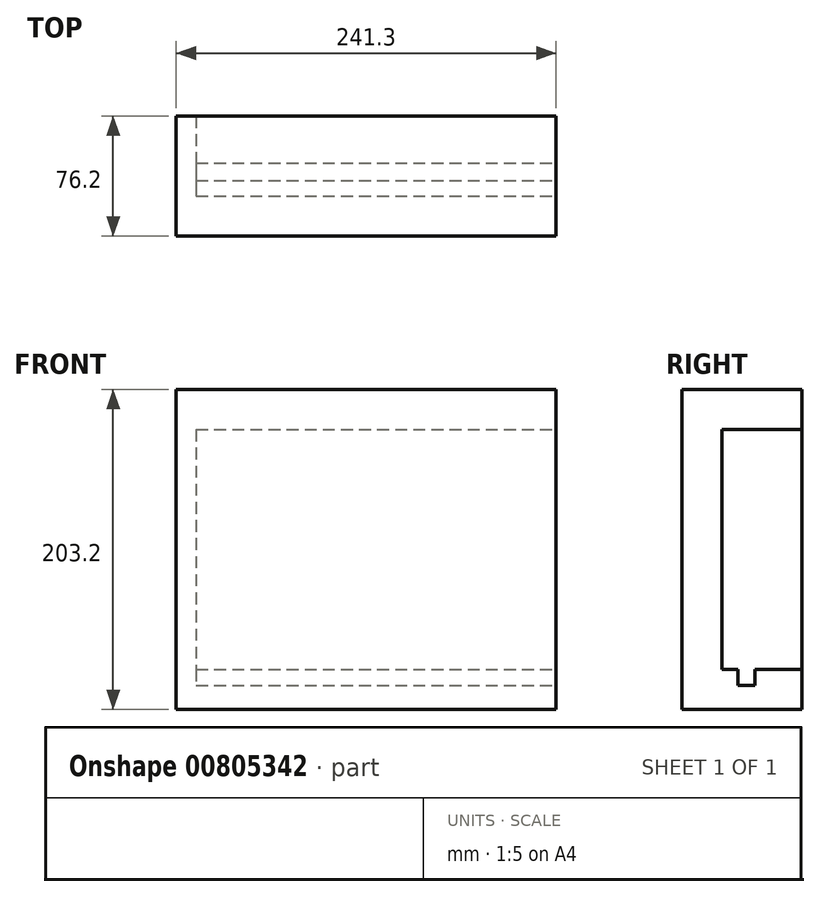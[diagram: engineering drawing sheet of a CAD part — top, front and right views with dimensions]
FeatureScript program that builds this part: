
annotation { "Feature Type Name" : "Feature", "Feature Type Description" : "" }
export const myFeature = defineFeature(function(context is Context, id is Id, definition is map)
    precondition{}
    {
        {
            var Q0;
            Q0=qCreatedBy(makeId("Top.planeOp"),FACE);
            var sketch = newSketch(context, id + "F0", { "sketchPlane" : qUnion([Q0])});
            skLineSegment(sketch, "E0.right", {"start": v(97.44, -125.76) * mm, "end": v(97.44, 52.04) * mm});
            skLineSegment(sketch, "E1.bottom", {"start": v(-131.16, 26.64) * mm, "end": v(97.44, 26.64) * mm});
            skLineSegment(sketch, "E1.top", {"start": v(-131.16, -24.16) * mm, "end": v(97.44, -24.16) * mm});
            skLineSegment(sketch, "E1.left", {"start": v(-131.16, 26.64) * mm, "end": v(-131.16, -24.16) * mm});
            skLineSegment(sketch, "E1.right", {"start": v(97.44, 26.64) * mm, "end": v(97.44, -24.16) * mm});
            skLineSegment(sketch, "E2.right", {"start": v(97.44, -49.56) * mm, "end": v(97.44, -100.36) * mm});
            skLineSegment(sketch, "E3.right", {"start": v(97.44, -80.36) * mm, "end": v(97.44, -90.36) * mm});
            skLineSegment(sketch, "E4.bottom", {"start": v(-131.16, -14.16) * mm, "end": v(97.44, -14.16) * mm});
            skLineSegment(sketch, "E4.top", {"start": v(-131.16, -3.16) * mm, "end": v(97.44, -3.16) * mm});
            skLineSegment(sketch, "E4.left", {"start": v(-131.16, -14.16) * mm, "end": v(-131.16, -3.16) * mm});
            skLineSegment(sketch, "E4.right", {"start": v(97.44, -14.16) * mm, "end": v(97.44, -3.16) * mm});
            skLineSegment(sketch, "E5.top", {"start": v(-143.86, -49.56) * mm, "end": v(97.44, -49.56) * mm});
            skLineSegment(sketch, "E5.right", {"start": v(97.44, 64.74) * mm, "end": v(97.44, -49.56) * mm});
            skLineSegment(sketch, "E6", {"start": v(-131.16, 26.64) * mm, "end": v(-143.86, 26.64) * mm});
            skLineSegment(sketch, "E7", {"start": v(-143.86, 26.64) * mm, "end": v(-143.86, -49.56) * mm});
            skSolve(sketch);
        }
        {
            var Q0;
            {var subQ0=sQuery(id+"F0.wireOp",EDGE,"E0.bottom");Q0=makeQuery(id+"F0.imprint","IMPRINT",FACE,{"disambiguationData":[TD([[makeQuery(id+"F0.imprint","IMPRINT",EDGE,{"derivedFrom":subQ0}),1.0]])]});}
            var Q1;
            {var subQ0=sQuery(id+"F0.wireOp",EDGE,"E1.top");Q1=makeQuery(id+"F0.imprint","IMPRINT",FACE,{"disambiguationData":[TD([[makeQuery(id+"F0.imprint","IMPRINT",EDGE,{"derivedFrom":subQ0}),-1.0]])]});}
            var Q2;
            {var subQ0=sQuery(id+"F0.wireOp",EDGE,"E0.top");Q2=makeQuery(id+"F0.imprint","IMPRINT",FACE,{"disambiguationData":[TD([[makeQuery(id+"F0.imprint","IMPRINT",EDGE,{"derivedFrom":subQ0}),-1.0]])]});}
            extrude(context, id + "F1", {"entities" : qUnion([Q0, Q1, Q2]), "depth" : 203.2 * mm, "offsetDistance" : 25.4 * mm});
        }
        {
            var Q0;
            {var subQ0=sQuery(id+"F0.wireOp",EDGE,"E2.top");Q0=makeQuery(id+"F0.imprint","IMPRINT",FACE,{"disambiguationData":[TD([[makeQuery(id+"F0.imprint","IMPRINT",EDGE,{"derivedFrom":subQ0}),1.0]])]});}
            var Q1;
            {var subQ0=sQuery(id+"F0.wireOp",EDGE,"E2.bottom");Q1=makeQuery(id+"F0.imprint","IMPRINT",FACE,{"disambiguationData":[TD([[makeQuery(id+"F0.imprint","IMPRINT",EDGE,{"derivedFrom":subQ0}),-1.0]])]});}
            var Q2;
            {var subQ0=sQuery(id+"F0.wireOp",EDGE,"E1.top");Q2=makeQuery(id+"F0.imprint","IMPRINT",FACE,{"disambiguationData":[TD([[makeQuery(id+"F0.imprint","IMPRINT",EDGE,{"derivedFrom":subQ0}),1.0]])]});}
            var Q3;
            {var subQ0=sQuery(id+"F0.wireOp",EDGE,"E1.bottom");Q3=makeQuery(id+"F0.imprint","IMPRINT",FACE,{"disambiguationData":[TD([[makeQuery(id+"F0.imprint","IMPRINT",EDGE,{"derivedFrom":subQ0}),-1.0]])]});}
            extrude(context, id + "F2", {"entities" : qUnion([Q0, Q1, Q2, Q3]), "depth" : 25.4 * mm, "offsetDistance" : 25.4 * mm});
        }
        {
            var Q0;
            Q0=makeQuery(id+"F0.imprint","IMPRINT",FACE,{"disambiguationData":[TD([[makeQuery(id+"F0.imprint","IMPRINT",EDGE,{"derivedFrom":sQuery(id+"F0.wireOp",EDGE,"E3.bottom")}),-1.0]])]});
            var Q1;
            Q1=makeQuery(id+"F0.imprint","IMPRINT",FACE,{"disambiguationData":[TD([[makeQuery(id+"F0.imprint","IMPRINT",EDGE,{"derivedFrom":sQuery(id+"F0.wireOp",EDGE,"E4.bottom")}),1.0]])]});
            extrude(context, id + "F3", {"entities" : qUnion([Q0, Q1]), "depth" : 15.24 * mm, "offsetDistance" : 25.4 * mm});
        }
        {
            var Q0;
            Q0=makeQuery(id+"F1.opExtrude","CAP_FACE",FACE,{"disambiguationData":[OSD([sQuery(id+"F0.wireOp",EDGE,"E1.top"),sQuery(id+"F0.wireOp",EDGE,"E1.left"),sQuery(id+"F0.wireOp",EDGE,"E4.left"),sQuery(id+"F0.wireOp",EDGE,"E5.top"),sQuery(id+"F0.wireOp",EDGE,"E5.right"),sQuery(id+"F0.wireOp",EDGE,"E6"),sQuery(id+"F0.wireOp",EDGE,"E7")])],"isStart":false});
            var sketch = newSketch(context, id + "F4", { "sketchPlane" : qUnion([Q0])});
            skLineSegment(sketch, "E8.bottom", {"start": v(97.44, -49.56) * mm, "end": v(-143.86, -49.56) * mm});
            skLineSegment(sketch, "E8.top", {"start": v(97.44, 26.64) * mm, "end": v(-143.86, 26.64) * mm});
            skLineSegment(sketch, "E8.left", {"start": v(97.44, -49.56) * mm, "end": v(97.44, 26.64) * mm});
            skLineSegment(sketch, "E8.right", {"start": v(-143.86, -49.56) * mm, "end": v(-143.86, 26.64) * mm});
            skSolve(sketch);
        }
        {
            var Q0;
            {var subQ4=makeQuery(id+"F1.opExtrude","CAP_EDGE",EDGE,{"disambiguationData":[OSD([sQuery(id+"F0.wireOp",EDGE,"E1.top")])],"isStart":false});Q0=makeQuery(id+"F4.imprint","IMPRINT",FACE,{"disambiguationData":[TD([[makeQuery(id+"F4.imprint","IMPRINT",EDGE,{"derivedFrom":subQ4}),1.0]])]});}
            extrude(context, id + "F5", {"entities" : qUnion([Q0]), "operationType" : NewBodyOperationType.ADD, "oppositeDirection" : true, "depth" : 25.4 * mm, "offsetDistance" : 25.4 * mm});
        }
        {
            var Q0;
            Q0=makeQuery(id+"F5.boolean.opBoolean","MERGE",FACE,{"derivedFrom":[makeQuery(id+"F1.opExtrude","SWEPT_FACE",FACE,{"disambiguationData":[OSD([sQuery(id+"F0.wireOp",EDGE,"E5.right")])]}),makeQuery(id+"F5.opExtrude","SWEPT_FACE",FACE,{"disambiguationData":[OSD([sQuery(id+"F4.wireOp",EDGE,"E8.left")])]})]});
            var sketch = newSketch(context, id + "F6", { "sketchPlane" : qUnion([Q0])});
            skLineSegment(sketch, "E9.bottom", {"start": v(-49.56, 0) * mm, "end": v(-16.4, 0) * mm});
            skLineSegment(sketch, "E9.top", {"start": v(-49.56, 23.35) * mm, "end": v(-16.4, 23.35) * mm});
            skLineSegment(sketch, "E9.left", {"start": v(-49.56, 0) * mm, "end": v(-49.56, 23.35) * mm});
            skLineSegment(sketch, "E9.right", {"start": v(-16.4, 0) * mm, "end": v(-16.4, 23.35) * mm});
            skSolve(sketch);
        }
        {
            var Q0;
            Q0 = qSketchRegion(id + "F6", true);
            extrude(context, id + "F7", {"entities" : qUnion([Q0]), "operationType" : NewBodyOperationType.ADD, "oppositeDirection" : true, "depth" : 25.4 * mm, "offsetDistance" : 25.4 * mm});
        }
        {
            var Q0;
            Q0=makeQuery(id+"F2.opExtrude","CAP_FACE",FACE,{"disambiguationData":[OSD([sQuery(id+"F0.wireOp",EDGE,"E1.bottom"),sQuery(id+"F0.wireOp",EDGE,"E1.left"),sQuery(id+"F0.wireOp",EDGE,"E4.top"),sQuery(id+"F0.wireOp",EDGE,"E5.right")])],"isStart":true});
            var sketch = newSketch(context, id + "F8", { "sketchPlane" : qUnion([Q0])});
            skLineSegment(sketch, "E10.bottom", {"start": v(97.44, -26.64) * mm, "end": v(-133.7, -26.64) * mm});
            skLineSegment(sketch, "E10.top", {"start": v(97.44, 33.38) * mm, "end": v(-133.7, 33.38) * mm});
            skLineSegment(sketch, "E10.left", {"start": v(97.44, -26.64) * mm, "end": v(97.44, 33.38) * mm});
            skLineSegment(sketch, "E10.right", {"start": v(-133.7, -26.64) * mm, "end": v(-133.7, 33.38) * mm});
            skSolve(sketch);
        }
        {
            var Q0;
            Q0 = qSketchRegion(id + "F8", true);
            extrude(context, id + "F9", {"entities" : qUnion([Q0]), "operationType" : NewBodyOperationType.ADD, "oppositeDirection" : true, "depth" : 0.25 * mm, "offsetDistance" : 25.4 * mm});
        }
    });
